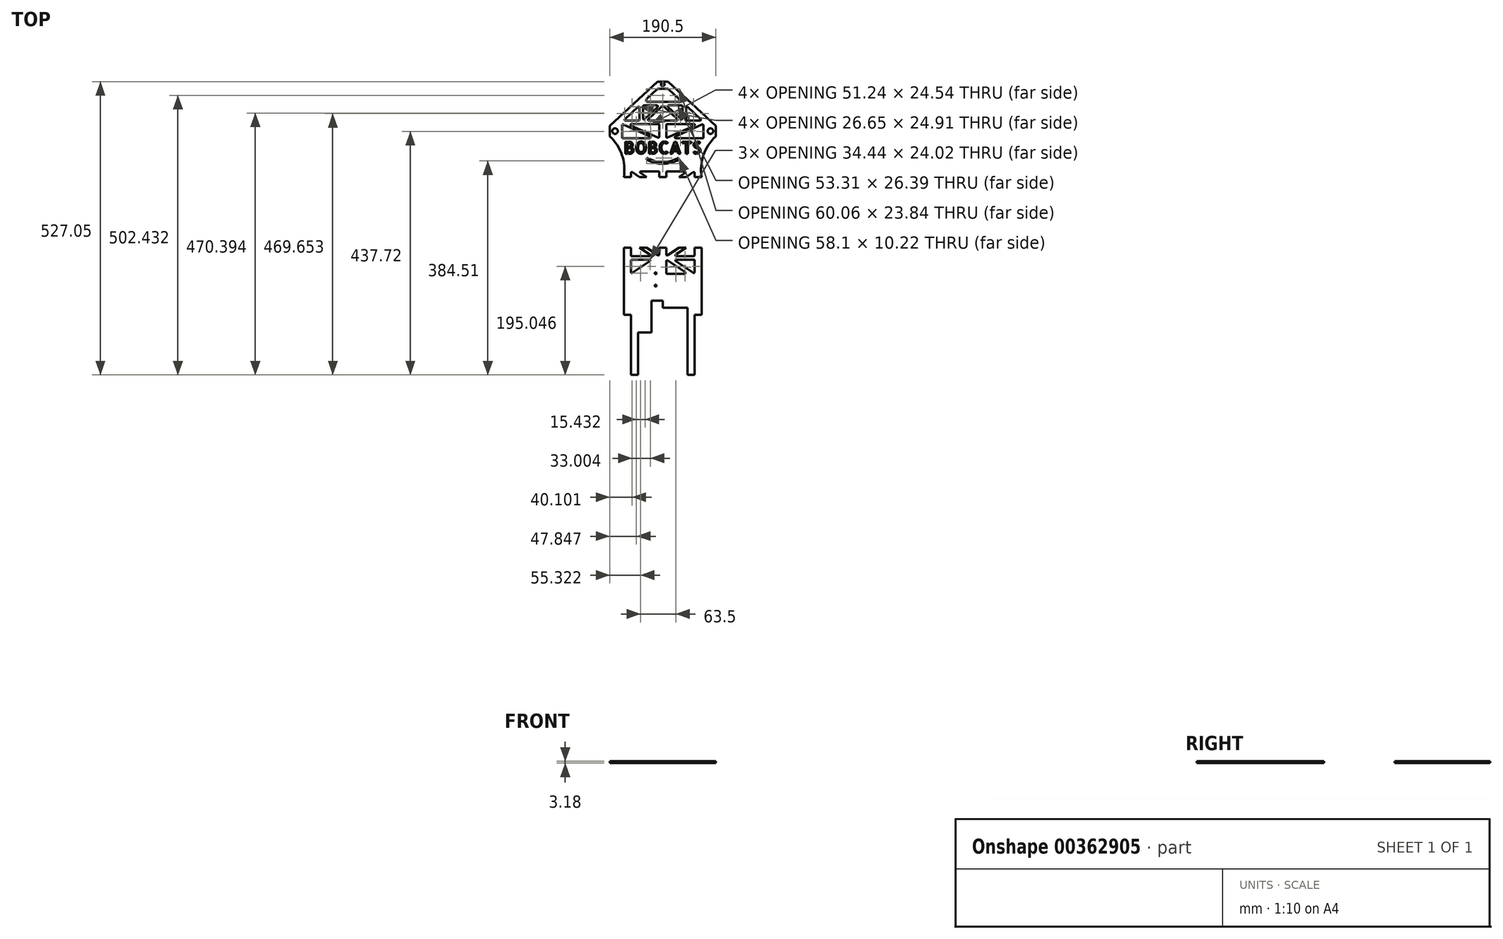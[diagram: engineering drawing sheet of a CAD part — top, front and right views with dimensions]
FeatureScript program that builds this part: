
annotation { "Feature Type Name" : "Feature", "Feature Type Description" : "" }
export const myFeature = defineFeature(function(context is Context, id is Id, definition is map)
    precondition{}
    {
        {
            var Q0;
            Q0=qCreatedBy(makeId("Top.planeOp"),FACE);
            var sketch = newSketch(context, id + "F0", { "sketchPlane" : qUnion([Q0])});
            skLineSegment(sketch, "E0.bottom", {"start": v(0, 0) * mm, "end": v(139.7, 0) * mm});
            skLineSegment(sketch, "E0.left", {"start": v(0, 0) * mm, "end": v(0, 127) * mm});
            skLineSegment(sketch, "E0.right", {"start": v(139.7, 0) * mm, "end": v(139.7, 153) * mm});
            skLineSegment(sketch, "E1.top", {"start": v(12.7, -228.6) * mm, "end": v(25.4, -228.6) * mm});
            skLineSegment(sketch, "E1.left", {"start": v(0, 0) * mm, "end": v(0, -120.65) * mm});
            skLineSegment(sketch, "E1.right", {"start": v(139.7, 0) * mm, "end": v(139.7, -120.65) * mm});
            skPoint(sketch, "E1.middle", {"position": v(69.85, -114.3) * mm});
            skLineSegment(sketch, "E2.top", {"start": v(25.4, -152.4) * mm, "end": v(49.53, -152.4) * mm});
            skLineSegment(sketch, "E2.left", {"start": v(25.4, -228.6) * mm, "end": v(25.4, -152.4) * mm});
            skLineSegment(sketch, "E2.right", {"start": v(114.3, -228.6) * mm, "end": v(114.3, -152.4) * mm});
            skLineSegment(sketch, "E3.top", {"start": v(114.3, -107.95) * mm, "end": v(69.85, -107.95) * mm});
            skLineSegment(sketch, "E3.left", {"start": v(114.3, -152.4) * mm, "end": v(114.3, -107.95) * mm});
            skLineSegment(sketch, "E4.top", {"start": v(69.85, -95.25) * mm, "end": v(49.53, -95.25) * mm});
            skLineSegment(sketch, "E4.left", {"start": v(69.85, -107.95) * mm, "end": v(69.85, -95.25) * mm});
            skLineSegment(sketch, "E4.right", {"start": v(49.53, -152.4) * mm, "end": v(49.53, -95.25) * mm});
            skLineSegment(sketch, "E5.left", {"start": v(25.4, -228.6) * mm, "end": v(25.4, -222.25) * mm});
            skLineSegment(sketch, "E5.right", {"start": v(114.3, -107.11) * mm, "end": v(114.3, -100.76) * mm});
            skPoint(sketch, "E6", {"position": v(57.15, -46.04) * mm});
            skPoint(sketch, "E7", {"position": v(57.15, -68.26) * mm});
            skCircle(sketch, "E8", {"center": v(57.15, -68.26) * mm, "radius": 1.59 * mm});
            skCircle(sketch, "E9", {"center": v(57.15, -46.04) * mm, "radius": 1.59 * mm});
            skLineSegment(sketch, "E10.top", {"start": v(0, -120.65) * mm, "end": v(12.7, -120.65) * mm});
            skLineSegment(sketch, "E10.right", {"start": v(12.7, -228.6) * mm, "end": v(12.7, -120.65) * mm});
            skPoint(sketch, "E11.oppositeSnap0", {"position": v(59.7, -152.4) * mm});
            skLineSegment(sketch, "E12.top", {"start": v(127, -120.65) * mm, "end": v(139.7, -120.65) * mm});
            skLineSegment(sketch, "E12.left", {"start": v(127, -228.6) * mm, "end": v(127, -120.65) * mm});
            skPoint(sketch, "E13.orphan", {"position": v(0, -228.6) * mm});
            skPoint(sketch, "E14.orphan", {"position": v(139.7, -228.6) * mm});
            skLineSegment(sketch, "E15.trimOffspring", {"start": v(114.3, -228.6) * mm, "end": v(127, -228.6) * mm});
            skPoint(sketch, "E3.bottom.end.orphan", {"position": v(69.85, -152.4) * mm});
            skLineSegment(sketch, "E16.bottom", {"start": v(60.32, 298.45) * mm, "end": v(79.38, 298.45) * mm});
            skLineSegment(sketch, "E16.top", {"start": v(0, 127) * mm, "end": v(139.7, 127) * mm});
            skLineSegment(sketch, "E16.left", {"start": v(-25.4, 219.08) * mm, "end": v(-25.4, 200.02) * mm});
            skLineSegment(sketch, "E16.right", {"start": v(165.1, 219.08) * mm, "end": v(165.1, 200.02) * mm});
            skLineSegment(sketch, "E17", {"start": v(60.32, 298.45) * mm, "end": v(-25.4, 219.08) * mm});
            skLineSegment(sketch, "E18", {"start": v(79.38, 298.45) * mm, "end": v(165.1, 219.08) * mm});
            skPoint(sketch, "E19", {"position": v(69.85, 293.37) * mm});
            skPoint(sketch, "E19.positionSnap0", {"position": v(69.85, 298.45) * mm});
            skCircle(sketch, "E20", {"center": v(69.85, 293.37) * mm, "radius": 3.2 * mm});
            skLineSegment(sketch, "E21.bottom", {"start": v(64.34, 298.45) * mm, "end": v(74.5, 298.45) * mm});
            skPoint(sketch, "E22", {"position": v(69.85, 127) * mm});
            skPoint(sketch, "E23", {"position": v(-25.4, 209.55) * mm});
            skPoint(sketch, "E24", {"position": v(165.1, 209.55) * mm});
            skText(sketch, "E25", { "text": "BOBCATS", "fontName": "AllertaStencil-Regular.ttf"});
            skArc(sketch, "E26", {"start": v(0, 127) * mm, "mid": v(-3.47, 166.72) * mm, "end": v(-25.4, 200.03) * mm});
            skLineSegment(sketch, "E27", {"start": v(42.39, 159.43) * mm, "end": v(100.33, 159.43) * mm, "construction": true});
            skArc(sketch, "E28", {"start": v(42.39, 159.43) * mm, "mid": v(69.85, 152.4) * mm, "end": v(97.31, 159.43) * mm, "construction": true});
            skArc(sketch, "E29.0", {"start": v(43.16, 160.83) * mm, "mid": v(69.85, 154) * mm, "end": v(96.54, 160.83) * mm});
            skArc(sketch, "E30.0", {"start": v(41.62, 158.03) * mm, "mid": v(69.85, 150.8) * mm, "end": v(98.08, 158.03) * mm});
            skCircle(sketch, "E31", {"center": v(42.39, 159.43) * mm, "radius": 1.6 * mm});
            skCircle(sketch, "E32", {"center": v(97.31, 159.43) * mm, "radius": 1.6 * mm});
            skLineSegment(sketch, "E33", {"start": v(59.72, 284.9) * mm, "end": v(40.83, 267.42) * mm});
            skLineSegment(sketch, "E34", {"start": v(42.99, 261.91) * mm, "end": v(96.71, 261.91) * mm});
            skLineSegment(sketch, "E35", {"start": v(98.87, 267.42) * mm, "end": v(79.98, 284.9) * mm});
            skLineSegment(sketch, "E36", {"start": v(77.83, 285.75) * mm, "end": v(61.87, 285.75) * mm});
            skPoint(sketch, "E37.visualSharp", {"position": v(60.63, 285.75) * mm});
            skArc(sketch, "E37.filletArc", {"start": v(61.87, 285.75) * mm, "mid": v(60.71, 285.53) * mm, "end": v(59.72, 284.9) * mm});
            skPoint(sketch, "E38.visualSharp", {"position": v(79.07, 285.75) * mm});
            skArc(sketch, "E38.filletArc", {"start": v(79.98, 284.9) * mm, "mid": v(78.99, 285.53) * mm, "end": v(77.83, 285.75) * mm});
            skPoint(sketch, "E39.visualSharp", {"position": v(34.89, 261.91) * mm});
            skArc(sketch, "E39.filletArc", {"start": v(40.83, 267.42) * mm, "mid": v(40.03, 263.93) * mm, "end": v(42.99, 261.91) * mm});
            skPoint(sketch, "E40.visualSharp", {"position": v(104.81, 261.91) * mm});
            skArc(sketch, "E40.filletArc", {"start": v(96.71, 261.91) * mm, "mid": v(99.67, 263.93) * mm, "end": v(98.87, 267.42) * mm});
            skCircle(sketch, "E41", {"center": v(-15.88, 209.55) * mm, "radius": 5 * mm});
            skCircle(sketch, "E42", {"center": v(155.58, 209.55) * mm, "radius": 5 * mm});
            skLineSegment(sketch, "E43", {"start": v(-3.18, 198.44) * mm, "end": v(-3.18, 219.8) * mm});
            skLineSegment(sketch, "E44", {"start": v(-0.94, 221.26) * mm, "end": v(47.14, 199.89) * mm});
            skLineSegment(sketch, "E45", {"start": v(46.5, 196.85) * mm, "end": v(-1.59, 196.85) * mm});
            skLineSegment(sketch, "E46", {"start": v(13.19, 219.21) * mm, "end": v(61.27, 197.84) * mm});
            skLineSegment(sketch, "E47", {"start": v(63.5, 199.3) * mm, "end": v(63.5, 220.66) * mm});
            skLineSegment(sketch, "E48", {"start": v(61.91, 222.25) * mm, "end": v(13.83, 222.25) * mm});
            skLineSegment(sketch, "E49", {"start": v(142.88, 198.44) * mm, "end": v(142.88, 219.8) * mm});
            skLineSegment(sketch, "E50", {"start": v(140.64, 221.26) * mm, "end": v(92.56, 199.89) * mm});
            skLineSegment(sketch, "E51", {"start": v(93.2, 196.85) * mm, "end": v(141.29, 196.85) * mm});
            skLineSegment(sketch, "E52", {"start": v(76.2, 199.3) * mm, "end": v(76.2, 220.66) * mm});
            skLineSegment(sketch, "E53", {"start": v(78.43, 197.84) * mm, "end": v(126.51, 219.21) * mm});
            skLineSegment(sketch, "E54", {"start": v(125.87, 222.25) * mm, "end": v(77.79, 222.25) * mm});
            skPoint(sketch, "E55.visualSharp", {"position": v(6.35, 222.25) * mm});
            skArc(sketch, "E55.filletArc", {"start": v(13.83, 222.25) * mm, "mid": v(12.28, 221) * mm, "end": v(13.19, 219.21) * mm});
            skPoint(sketch, "E56.visualSharp", {"position": v(53.98, 196.85) * mm});
            skArc(sketch, "E56.filletArc", {"start": v(46.5, 196.85) * mm, "mid": v(48.05, 198.1) * mm, "end": v(47.14, 199.89) * mm});
            skPoint(sketch, "E57.visualSharp", {"position": v(-3.18, 222.25) * mm});
            skArc(sketch, "E57.filletArc", {"start": v(-0.94, 221.26) * mm, "mid": v(-2.45, 221.14) * mm, "end": v(-3.18, 219.8) * mm});
            skPoint(sketch, "E58.visualSharp", {"position": v(-3.18, 196.85) * mm});
            skArc(sketch, "E58.filletArc", {"start": v(-3.18, 198.44) * mm, "mid": v(-2.71, 197.31) * mm, "end": v(-1.59, 196.85) * mm});
            skPoint(sketch, "E59.visualSharp", {"position": v(76.2, 222.25) * mm});
            skArc(sketch, "E59.filletArc", {"start": v(77.79, 222.25) * mm, "mid": v(76.66, 221.79) * mm, "end": v(76.2, 220.66) * mm});
            skPoint(sketch, "E60.visualSharp", {"position": v(63.5, 222.25) * mm});
            skArc(sketch, "E60.filletArc", {"start": v(63.5, 220.66) * mm, "mid": v(63.04, 221.79) * mm, "end": v(61.91, 222.25) * mm});
            skPoint(sketch, "E61.visualSharp", {"position": v(63.5, 196.85) * mm});
            skArc(sketch, "E61.filletArc", {"start": v(61.27, 197.84) * mm, "mid": v(62.78, 197.96) * mm, "end": v(63.5, 199.3) * mm});
            skPoint(sketch, "E62.visualSharp", {"position": v(76.2, 196.85) * mm});
            skArc(sketch, "E62.filletArc", {"start": v(76.2, 199.3) * mm, "mid": v(76.92, 197.96) * mm, "end": v(78.43, 197.84) * mm});
            skPoint(sketch, "E63.visualSharp", {"position": v(133.35, 222.25) * mm});
            skArc(sketch, "E63.filletArc", {"start": v(126.51, 219.21) * mm, "mid": v(127.42, 221) * mm, "end": v(125.87, 222.25) * mm});
            skPoint(sketch, "E64.visualSharp", {"position": v(85.72, 196.85) * mm});
            skArc(sketch, "E64.filletArc", {"start": v(92.56, 199.89) * mm, "mid": v(91.65, 198.1) * mm, "end": v(93.2, 196.85) * mm});
            skPoint(sketch, "E65.visualSharp", {"position": v(142.88, 222.25) * mm});
            skArc(sketch, "E65.filletArc", {"start": v(142.88, 219.8) * mm, "mid": v(142.15, 221.14) * mm, "end": v(140.64, 221.26) * mm});
            skPoint(sketch, "E66.visualSharp", {"position": v(142.88, 196.85) * mm});
            skArc(sketch, "E66.filletArc", {"start": v(141.29, 196.85) * mm, "mid": v(142.41, 197.31) * mm, "end": v(142.88, 198.44) * mm});
            skLineSegment(sketch, "E67", {"start": v(68.77, 254.57) * mm, "end": v(43.7, 231.35) * mm});
            skLineSegment(sketch, "E68", {"start": v(44.78, 228.6) * mm, "end": v(94.92, 228.6) * mm});
            skLineSegment(sketch, "E69", {"start": v(96, 231.35) * mm, "end": v(70.93, 254.57) * mm});
            skLineSegment(sketch, "E70", {"start": v(60.53, 252.81) * mm, "end": v(37.04, 231.07) * mm});
            skLineSegment(sketch, "E71", {"start": v(34.38, 232.23) * mm, "end": v(34.38, 253.98) * mm});
            skLineSegment(sketch, "E72", {"start": v(35.97, 255.56) * mm, "end": v(59.45, 255.56) * mm});
            skLineSegment(sketch, "E73", {"start": v(25.36, 253.1) * mm, "end": v(1.88, 231.35) * mm});
            skLineSegment(sketch, "E74", {"start": v(2.96, 228.6) * mm, "end": v(26.44, 228.6) * mm});
            skLineSegment(sketch, "E75", {"start": v(28.03, 230.19) * mm, "end": v(28.03, 251.93) * mm});
            skPoint(sketch, "E76.visualSharp", {"position": v(28.03, 255.56) * mm});
            skArc(sketch, "E76.filletArc", {"start": v(28.03, 251.93) * mm, "mid": v(27.08, 253.39) * mm, "end": v(25.36, 253.1) * mm});
            skPoint(sketch, "E77.visualSharp", {"position": v(-1.1, 228.6) * mm});
            skArc(sketch, "E77.filletArc", {"start": v(1.88, 231.35) * mm, "mid": v(1.48, 229.6) * mm, "end": v(2.96, 228.6) * mm});
            skPoint(sketch, "E78.visualSharp", {"position": v(28.03, 228.6) * mm});
            skArc(sketch, "E78.filletArc", {"start": v(26.44, 228.6) * mm, "mid": v(27.56, 229.06) * mm, "end": v(28.03, 230.19) * mm});
            skPoint(sketch, "E79.visualSharp", {"position": v(34.38, 228.6) * mm});
            skArc(sketch, "E79.filletArc", {"start": v(34.38, 232.23) * mm, "mid": v(35.33, 230.78) * mm, "end": v(37.04, 231.07) * mm});
            skPoint(sketch, "E80.visualSharp", {"position": v(34.38, 255.56) * mm});
            skArc(sketch, "E80.filletArc", {"start": v(35.97, 255.56) * mm, "mid": v(34.84, 255.1) * mm, "end": v(34.38, 253.98) * mm});
            skPoint(sketch, "E81.visualSharp", {"position": v(63.5, 255.56) * mm});
            skArc(sketch, "E81.filletArc", {"start": v(60.53, 252.81) * mm, "mid": v(60.93, 254.56) * mm, "end": v(59.45, 255.56) * mm});
            skPoint(sketch, "E82.visualSharp", {"position": v(69.85, 255.56) * mm});
            skArc(sketch, "E82.filletArc", {"start": v(70.93, 254.57) * mm, "mid": v(69.85, 254.99) * mm, "end": v(68.77, 254.57) * mm});
            skPoint(sketch, "E83.visualSharp", {"position": v(40.73, 228.6) * mm});
            skArc(sketch, "E83.filletArc", {"start": v(43.7, 231.35) * mm, "mid": v(43.3, 229.6) * mm, "end": v(44.78, 228.6) * mm});
            skPoint(sketch, "E84.visualSharp", {"position": v(98.97, 228.6) * mm});
            skArc(sketch, "E84.filletArc", {"start": v(94.92, 228.6) * mm, "mid": v(96.4, 229.6) * mm, "end": v(96, 231.35) * mm});
            skLineSegment(sketch, "E85", {"start": v(69.85, 260.44) * mm, "end": v(69.85, 219.43) * mm});
            skLineSegment(sketch, "E86.MirrorCS", {"start": v(79.17, 252.81) * mm, "end": v(102.66, 231.07) * mm});
            skLineSegment(sketch, "E87.MirrorCS", {"start": v(103.73, 255.56) * mm, "end": v(80.25, 255.56) * mm});
            skLineSegment(sketch, "E88.MirrorCS", {"start": v(105.32, 232.23) * mm, "end": v(105.32, 253.98) * mm});
            skLineSegment(sketch, "E89.MirrorCS", {"start": v(111.67, 230.19) * mm, "end": v(111.67, 251.93) * mm});
            skLineSegment(sketch, "E90.MirrorCS", {"start": v(114.34, 253.1) * mm, "end": v(137.82, 231.35) * mm});
            skLineSegment(sketch, "E91.MirrorCS", {"start": v(136.74, 228.6) * mm, "end": v(113.26, 228.6) * mm});
            skArc(sketch, "E92.MirrorCS", {"start": v(111.67, 251.93) * mm, "mid": v(112.62, 253.39) * mm, "end": v(114.34, 253.1) * mm});
            skArc(sketch, "E93.MirrorCS", {"start": v(113.26, 228.6) * mm, "mid": v(112.14, 229.06) * mm, "end": v(111.67, 230.19) * mm});
            skArc(sketch, "E94.MirrorCS", {"start": v(105.32, 232.23) * mm, "mid": v(104.37, 230.78) * mm, "end": v(102.66, 231.07) * mm});
            skArc(sketch, "E95.MirrorCS", {"start": v(103.73, 255.56) * mm, "mid": v(104.86, 255.1) * mm, "end": v(105.32, 253.98) * mm});
            skArc(sketch, "E96.MirrorCS", {"start": v(79.17, 252.81) * mm, "mid": v(78.77, 254.56) * mm, "end": v(80.25, 255.56) * mm});
            skArc(sketch, "E97.MirrorCS", {"start": v(137.82, 231.35) * mm, "mid": v(138.22, 229.6) * mm, "end": v(136.74, 228.6) * mm});
            skLineSegment(sketch, "E98", {"start": v(12.7, 113.4) * mm, "end": v(12.7, 134.24) * mm});
            skLineSegment(sketch, "E99", {"start": v(15.17, 135.56) * mm, "end": v(46.44, 114.71) * mm});
            skLineSegment(sketch, "E100", {"start": v(45.56, 111.8) * mm, "end": v(14.29, 111.8) * mm});
            skLineSegment(sketch, "E101", {"start": v(29.76, 134.3) * mm, "end": v(61.03, 113.45) * mm});
            skLineSegment(sketch, "E102", {"start": v(63.5, 114.77) * mm, "end": v(63.5, 135.62) * mm});
            skLineSegment(sketch, "E103", {"start": v(61.91, 137.2) * mm, "end": v(30.64, 137.2) * mm});
            skLineSegment(sketch, "E104", {"start": v(76.2, 135.62) * mm, "end": v(76.2, 114.77) * mm});
            skLineSegment(sketch, "E105", {"start": v(78.67, 113.45) * mm, "end": v(109.94, 134.3) * mm});
            skLineSegment(sketch, "E106", {"start": v(109.06, 137.2) * mm, "end": v(77.79, 137.2) * mm});
            skLineSegment(sketch, "E107", {"start": v(124.53, 135.56) * mm, "end": v(93.26, 114.71) * mm});
            skLineSegment(sketch, "E108", {"start": v(94.14, 111.8) * mm, "end": v(125.41, 111.8) * mm});
            skLineSegment(sketch, "E109", {"start": v(127, 113.4) * mm, "end": v(127, 134.24) * mm});
            skArc(sketch, "E110.MirrorCS", {"start": v(139.7, 127) * mm, "mid": v(143.17, 166.72) * mm, "end": v(165.1, 200.03) * mm});
            skLineSegment(sketch, "E111", {"start": v(14.29, 105.46) * mm, "end": v(45.56, 105.46) * mm});
            skLineSegment(sketch, "E112", {"start": v(46.44, 102.55) * mm, "end": v(15.17, 81.7) * mm});
            skLineSegment(sketch, "E113", {"start": v(12.7, 83.02) * mm, "end": v(12.7, 103.87) * mm});
            skLineSegment(sketch, "E114", {"start": v(63.5, 102.61) * mm, "end": v(63.5, 81.64) * mm});
            skLineSegment(sketch, "E115", {"start": v(61.91, 80.06) * mm, "end": v(27.83, 80.06) * mm});
            skLineSegment(sketch, "E116", {"start": v(27, 83) * mm, "end": v(61.08, 103.97) * mm});
            skLineSegment(sketch, "E117", {"start": v(76.2, 102.49) * mm, "end": v(76.2, 81.64) * mm});
            skLineSegment(sketch, "E118", {"start": v(77.79, 80.06) * mm, "end": v(109.06, 80.06) * mm});
            skLineSegment(sketch, "E119", {"start": v(109.94, 82.96) * mm, "end": v(78.67, 103.8) * mm});
            skLineSegment(sketch, "E120", {"start": v(93.26, 102.55) * mm, "end": v(124.53, 81.7) * mm});
            skLineSegment(sketch, "E121", {"start": v(127, 83.02) * mm, "end": v(127, 103.87) * mm});
            skLineSegment(sketch, "E122", {"start": v(125.41, 105.46) * mm, "end": v(94.14, 105.46) * mm});
            skPoint(sketch, "E123.visualSharp", {"position": v(12.7, 111.8) * mm});
            skArc(sketch, "E123.filletArc", {"start": v(12.7, 113.4) * mm, "mid": v(13.16, 112.27) * mm, "end": v(14.29, 111.8) * mm});
            skPoint(sketch, "E124.visualSharp", {"position": v(50.8, 111.8) * mm});
            skArc(sketch, "E124.filletArc", {"start": v(45.56, 111.8) * mm, "mid": v(47.08, 112.93) * mm, "end": v(46.44, 114.71) * mm});
            skPoint(sketch, "E125.visualSharp", {"position": v(12.7, 137.2) * mm});
            skArc(sketch, "E125.filletArc", {"start": v(15.17, 135.56) * mm, "mid": v(13.54, 135.64) * mm, "end": v(12.7, 134.24) * mm});
            skPoint(sketch, "E126.visualSharp", {"position": v(25.4, 137.2) * mm});
            skArc(sketch, "E126.filletArc", {"start": v(30.64, 137.2) * mm, "mid": v(29.12, 136.08) * mm, "end": v(29.76, 134.3) * mm});
            skPoint(sketch, "E127.visualSharp", {"position": v(63.5, 137.2) * mm});
            skArc(sketch, "E127.filletArc", {"start": v(63.5, 135.62) * mm, "mid": v(63.04, 136.74) * mm, "end": v(61.91, 137.2) * mm});
            skPoint(sketch, "E128.visualSharp", {"position": v(63.5, 111.8) * mm});
            skArc(sketch, "E128.filletArc", {"start": v(61.03, 113.45) * mm, "mid": v(62.66, 113.37) * mm, "end": v(63.5, 114.77) * mm});
            skPoint(sketch, "E129.visualSharp", {"position": v(76.2, 111.8) * mm});
            skArc(sketch, "E129.filletArc", {"start": v(76.2, 114.77) * mm, "mid": v(77.04, 113.37) * mm, "end": v(78.67, 113.45) * mm});
            skPoint(sketch, "E130.visualSharp", {"position": v(114.3, 137.2) * mm});
            skArc(sketch, "E130.filletArc", {"start": v(109.94, 134.3) * mm, "mid": v(110.58, 136.08) * mm, "end": v(109.06, 137.2) * mm});
            skPoint(sketch, "E131.visualSharp", {"position": v(76.2, 137.2) * mm});
            skArc(sketch, "E131.filletArc", {"start": v(77.79, 137.2) * mm, "mid": v(76.66, 136.74) * mm, "end": v(76.2, 135.62) * mm});
            skPoint(sketch, "E132.visualSharp", {"position": v(127, 137.2) * mm});
            skArc(sketch, "E132.filletArc", {"start": v(127, 134.24) * mm, "mid": v(126.16, 135.64) * mm, "end": v(124.53, 135.56) * mm});
            skPoint(sketch, "E133.visualSharp", {"position": v(88.9, 111.8) * mm});
            skArc(sketch, "E133.filletArc", {"start": v(93.26, 114.71) * mm, "mid": v(92.62, 112.93) * mm, "end": v(94.14, 111.8) * mm});
            skPoint(sketch, "E134.visualSharp", {"position": v(127, 111.8) * mm});
            skArc(sketch, "E134.filletArc", {"start": v(125.41, 111.8) * mm, "mid": v(126.54, 112.27) * mm, "end": v(127, 113.4) * mm});
            skPoint(sketch, "E135.visualSharp", {"position": v(12.7, 105.46) * mm});
            skArc(sketch, "E135.filletArc", {"start": v(14.29, 105.46) * mm, "mid": v(13.16, 105) * mm, "end": v(12.7, 103.87) * mm});
            skPoint(sketch, "E136.visualSharp", {"position": v(50.8, 105.46) * mm});
            skArc(sketch, "E136.filletArc", {"start": v(46.44, 102.55) * mm, "mid": v(47.08, 104.33) * mm, "end": v(45.56, 105.46) * mm});
            skPoint(sketch, "E137.visualSharp", {"position": v(63.5, 105.46) * mm});
            skArc(sketch, "E137.filletArc", {"start": v(63.5, 102.61) * mm, "mid": v(62.69, 104) * mm, "end": v(61.08, 103.97) * mm});
            skPoint(sketch, "E138.visualSharp", {"position": v(63.5, 80.06) * mm});
            skArc(sketch, "E138.filletArc", {"start": v(61.91, 80.06) * mm, "mid": v(63.04, 80.52) * mm, "end": v(63.5, 81.64) * mm});
            skPoint(sketch, "E139.visualSharp", {"position": v(22.23, 80.06) * mm});
            skArc(sketch, "E139.filletArc", {"start": v(27, 83) * mm, "mid": v(26.3, 81.21) * mm, "end": v(27.83, 80.06) * mm});
            skPoint(sketch, "E140.visualSharp", {"position": v(76.2, 80.06) * mm});
            skArc(sketch, "E140.filletArc", {"start": v(76.2, 81.64) * mm, "mid": v(76.66, 80.52) * mm, "end": v(77.79, 80.06) * mm});
            skPoint(sketch, "E141.visualSharp", {"position": v(114.3, 80.06) * mm});
            skArc(sketch, "E141.filletArc", {"start": v(109.06, 80.06) * mm, "mid": v(110.58, 81.18) * mm, "end": v(109.94, 82.96) * mm});
            skPoint(sketch, "E142.visualSharp", {"position": v(76.2, 105.46) * mm});
            skArc(sketch, "E142.filletArc", {"start": v(78.67, 103.8) * mm, "mid": v(77.04, 103.89) * mm, "end": v(76.2, 102.49) * mm});
            skPoint(sketch, "E143.visualSharp", {"position": v(88.9, 105.46) * mm});
            skArc(sketch, "E143.filletArc", {"start": v(94.14, 105.46) * mm, "mid": v(92.62, 104.33) * mm, "end": v(93.26, 102.55) * mm});
            skPoint(sketch, "E144.visualSharp", {"position": v(127, 105.46) * mm});
            skArc(sketch, "E144.filletArc", {"start": v(127, 103.87) * mm, "mid": v(126.54, 105) * mm, "end": v(125.41, 105.46) * mm});
            skPoint(sketch, "E145.visualSharp", {"position": v(127, 80.06) * mm});
            skArc(sketch, "E145.filletArc", {"start": v(124.53, 81.7) * mm, "mid": v(126.16, 81.62) * mm, "end": v(127, 83.02) * mm});
            skPoint(sketch, "E146.visualSharp", {"position": v(12.7, 80.06) * mm});
            skArc(sketch, "E146.filletArc", {"start": v(12.7, 83.02) * mm, "mid": v(13.54, 81.62) * mm, "end": v(15.17, 81.7) * mm});
            skLineSegment(sketch, "E147.0.1.0", {"start": v(127, 19.52) * mm, "end": v(127, 40.37) * mm});
            skArc(sketch, "E147.0.1.1", {"start": v(109.06, 16.56) * mm, "mid": v(110.58, 17.68) * mm, "end": v(109.94, 19.46) * mm});
            skPoint(sketch, "E147.0.1.2", {"position": v(88.9, 41.96) * mm});
            skLineSegment(sketch, "E147.0.1.3", {"start": v(127, 49.9) * mm, "end": v(127, 70.74) * mm});
            skLineSegment(sketch, "E147.0.1.4", {"start": v(45.56, 48.3) * mm, "end": v(14.29, 48.3) * mm});
            skLineSegment(sketch, "E147.0.1.5", {"start": v(61.91, 73.7) * mm, "end": v(30.64, 73.7) * mm});
            skArc(sketch, "E147.0.1.6", {"start": v(94.14, 41.96) * mm, "mid": v(92.62, 40.83) * mm, "end": v(93.26, 39.05) * mm});
            skLineSegment(sketch, "E147.0.1.7", {"start": v(77.79, 16.56) * mm, "end": v(109.06, 16.56) * mm});
            skPoint(sketch, "E147.0.1.8", {"position": v(127, 41.96) * mm});
            skPoint(sketch, "E147.0.1.9", {"position": v(76.2, 73.7) * mm});
            skPoint(sketch, "E147.0.1.10", {"position": v(127, 16.56) * mm});
            skPoint(sketch, "E147.0.1.11", {"position": v(63.5, 41.96) * mm});
            skArc(sketch, "E147.0.1.12", {"start": v(45.56, 48.3) * mm, "mid": v(47.08, 49.43) * mm, "end": v(46.44, 51.21) * mm});
            skLineSegment(sketch, "E147.0.1.13", {"start": v(124.53, 72.06) * mm, "end": v(93.26, 51.21) * mm});
            skPoint(sketch, "E147.0.1.14", {"position": v(22.23, 16.56) * mm});
            skPoint(sketch, "E147.0.1.15", {"position": v(63.5, 48.3) * mm});
            skArc(sketch, "E147.0.1.16", {"start": v(61.03, 49.95) * mm, "mid": v(62.66, 49.87) * mm, "end": v(63.5, 51.27) * mm});
            skPoint(sketch, "E147.0.1.17", {"position": v(25.4, 73.7) * mm});
            skPoint(sketch, "E147.0.1.18", {"position": v(63.5, 16.56) * mm});
            skLineSegment(sketch, "E147.0.1.19", {"start": v(61.91, 16.56) * mm, "end": v(27.83, 16.56) * mm});
            skLineSegment(sketch, "E147.0.1.20", {"start": v(29.76, 70.8) * mm, "end": v(61.03, 49.95) * mm});
            skLineSegment(sketch, "E147.0.1.21", {"start": v(63.5, 39.11) * mm, "end": v(63.5, 18.14) * mm});
            skPoint(sketch, "E147.0.1.22", {"position": v(76.2, 48.3) * mm});
            skLineSegment(sketch, "E147.0.1.23", {"start": v(125.41, 41.96) * mm, "end": v(94.14, 41.96) * mm});
            skPoint(sketch, "E147.0.1.24", {"position": v(12.7, 41.96) * mm});
            skArc(sketch, "E147.0.1.25", {"start": v(12.7, 19.52) * mm, "mid": v(13.54, 18.12) * mm, "end": v(15.17, 18.2) * mm});
            skPoint(sketch, "E147.0.1.26", {"position": v(69.85, 63.5) * mm});
            skLineSegment(sketch, "E147.0.1.27", {"start": v(27, 19.5) * mm, "end": v(61.08, 40.47) * mm});
            skLineSegment(sketch, "E147.0.1.28", {"start": v(63.5, 51.27) * mm, "end": v(63.5, 72.12) * mm});
            skPoint(sketch, "E147.0.1.29", {"position": v(12.7, 16.56) * mm});
            skPoint(sketch, "E147.0.1.30", {"position": v(76.2, 41.96) * mm});
            skArc(sketch, "E147.0.1.31", {"start": v(15.17, 72.06) * mm, "mid": v(13.54, 72.14) * mm, "end": v(12.7, 70.74) * mm});
            skPoint(sketch, "E147.0.1.32", {"position": v(127, 73.7) * mm});
            skArc(sketch, "E147.0.1.33", {"start": v(63.5, 39.11) * mm, "mid": v(62.69, 40.5) * mm, "end": v(61.08, 40.47) * mm});
            skLineSegment(sketch, "E147.0.1.34", {"start": v(14.29, 41.96) * mm, "end": v(45.56, 41.96) * mm});
            skLineSegment(sketch, "E147.0.1.35", {"start": v(109.06, 73.7) * mm, "end": v(77.79, 73.7) * mm});
            skPoint(sketch, "E147.0.1.36", {"position": v(114.3, 16.56) * mm});
            skLineSegment(sketch, "E147.0.1.37", {"start": v(46.44, 39.05) * mm, "end": v(15.17, 18.2) * mm});
            skPoint(sketch, "E147.0.1.38", {"position": v(63.5, 73.7) * mm});
            skPoint(sketch, "E147.0.1.39", {"position": v(76.2, 16.56) * mm});
            skArc(sketch, "E147.0.1.40", {"start": v(124.53, 18.2) * mm, "mid": v(126.16, 18.12) * mm, "end": v(127, 19.52) * mm});
            skPoint(sketch, "E147.0.1.41", {"position": v(12.7, 73.7) * mm});
            skPoint(sketch, "E147.0.1.42", {"position": v(50.8, 48.3) * mm});
            skLineSegment(sketch, "E147.0.1.43", {"start": v(94.14, 48.3) * mm, "end": v(125.41, 48.3) * mm});
            skPoint(sketch, "E147.0.1.44", {"position": v(88.9, 48.3) * mm});
            skLineSegment(sketch, "E147.0.1.45", {"start": v(12.7, 49.9) * mm, "end": v(12.7, 70.74) * mm});
            skPoint(sketch, "E147.0.1.46", {"position": v(114.3, 73.7) * mm});
            skPoint(sketch, "E147.0.1.47", {"position": v(50.8, 41.96) * mm});
            skLineSegment(sketch, "E147.0.1.48", {"start": v(109.94, 19.46) * mm, "end": v(78.67, 40.3) * mm});
            skArc(sketch, "E147.0.1.49", {"start": v(78.67, 40.3) * mm, "mid": v(77.04, 40.39) * mm, "end": v(76.2, 38.99) * mm});
            skPoint(sketch, "E147.0.1.50", {"position": v(127, 48.3) * mm});
            skArc(sketch, "E147.0.1.51", {"start": v(127, 70.74) * mm, "mid": v(126.16, 72.14) * mm, "end": v(124.53, 72.06) * mm});
            skLineSegment(sketch, "E147.0.1.52", {"start": v(93.26, 39.05) * mm, "end": v(124.53, 18.2) * mm});
            skLineSegment(sketch, "E147.0.1.53", {"start": v(78.67, 49.95) * mm, "end": v(109.94, 70.8) * mm});
            skArc(sketch, "E147.0.1.54", {"start": v(46.44, 39.05) * mm, "mid": v(47.08, 40.83) * mm, "end": v(45.56, 41.96) * mm});
            skLineSegment(sketch, "E147.0.1.55", {"start": v(15.17, 72.06) * mm, "end": v(46.44, 51.21) * mm});
            skArc(sketch, "E147.0.1.56", {"start": v(27, 19.5) * mm, "mid": v(26.3, 17.71) * mm, "end": v(27.83, 16.56) * mm});
            skArc(sketch, "E147.0.1.57", {"start": v(93.26, 51.21) * mm, "mid": v(92.62, 49.43) * mm, "end": v(94.14, 48.3) * mm});
            skPoint(sketch, "E147.0.1.58", {"position": v(12.7, 48.3) * mm});
            skLineSegment(sketch, "E147.0.1.59", {"start": v(76.2, 72.12) * mm, "end": v(76.2, 51.27) * mm});
            skLineSegment(sketch, "E147.0.1.60", {"start": v(76.2, 38.99) * mm, "end": v(76.2, 18.14) * mm});
            skLineSegment(sketch, "E147.0.1.61", {"start": v(12.7, 19.52) * mm, "end": v(12.7, 40.37) * mm});
            skArc(sketch, "E147.0.1.62", {"start": v(76.2, 51.27) * mm, "mid": v(77.04, 49.87) * mm, "end": v(78.67, 49.95) * mm});
            skArc(sketch, "E147.0.1.63", {"start": v(12.7, 49.9) * mm, "mid": v(13.16, 48.77) * mm, "end": v(14.29, 48.3) * mm});
            skArc(sketch, "E147.0.1.64", {"start": v(14.29, 41.96) * mm, "mid": v(13.16, 41.5) * mm, "end": v(12.7, 40.37) * mm});
            skArc(sketch, "E147.0.1.65", {"start": v(127, 40.37) * mm, "mid": v(126.54, 41.5) * mm, "end": v(125.41, 41.96) * mm});
            skArc(sketch, "E147.0.1.66", {"start": v(109.94, 70.8) * mm, "mid": v(110.58, 72.58) * mm, "end": v(109.06, 73.7) * mm});
            skArc(sketch, "E147.0.1.67", {"start": v(61.91, 16.56) * mm, "mid": v(63.04, 17.02) * mm, "end": v(63.5, 18.14) * mm});
            skArc(sketch, "E147.0.1.68", {"start": v(30.64, 73.7) * mm, "mid": v(29.12, 72.58) * mm, "end": v(29.76, 70.8) * mm});
            skArc(sketch, "E147.0.1.69", {"start": v(63.5, 72.12) * mm, "mid": v(63.04, 73.24) * mm, "end": v(61.91, 73.7) * mm});
            skArc(sketch, "E147.0.1.70", {"start": v(77.79, 73.7) * mm, "mid": v(76.66, 73.24) * mm, "end": v(76.2, 72.12) * mm});
            skArc(sketch, "E147.0.1.71", {"start": v(76.2, 18.14) * mm, "mid": v(76.66, 17.02) * mm, "end": v(77.79, 16.56) * mm});
            skArc(sketch, "E147.0.1.72", {"start": v(125.41, 48.3) * mm, "mid": v(126.54, 48.77) * mm, "end": v(127, 49.9) * mm});
            skLineSegment(sketch, "E147.0.2.0", {"start": v(127, -43.98) * mm, "end": v(127, -23.13) * mm});
            skArc(sketch, "E147.0.2.1", {"start": v(109.06, -46.94) * mm, "mid": v(110.58, -45.82) * mm, "end": v(109.94, -44.04) * mm});
            skPoint(sketch, "E147.0.2.2", {"position": v(88.9, -21.54) * mm});
            skLineSegment(sketch, "E147.0.2.3", {"start": v(127, -13.6) * mm, "end": v(127, 7.24) * mm});
            skLineSegment(sketch, "E147.0.2.4", {"start": v(45.56, -15.2) * mm, "end": v(14.29, -15.2) * mm});
            skLineSegment(sketch, "E147.0.2.5", {"start": v(61.91, 10.2) * mm, "end": v(30.64, 10.2) * mm});
            skArc(sketch, "E147.0.2.6", {"start": v(94.14, -21.54) * mm, "mid": v(92.62, -22.67) * mm, "end": v(93.26, -24.45) * mm});
            skLineSegment(sketch, "E147.0.2.7", {"start": v(77.79, -46.94) * mm, "end": v(109.06, -46.94) * mm});
            skPoint(sketch, "E147.0.2.8", {"position": v(127, -21.54) * mm});
            skPoint(sketch, "E147.0.2.9", {"position": v(76.2, 10.2) * mm});
            skPoint(sketch, "E147.0.2.10", {"position": v(127, -46.94) * mm});
            skPoint(sketch, "E147.0.2.11", {"position": v(63.5, -21.54) * mm});
            skArc(sketch, "E147.0.2.12", {"start": v(45.56, -15.2) * mm, "mid": v(47.08, -14.07) * mm, "end": v(46.44, -12.29) * mm});
            skLineSegment(sketch, "E147.0.2.13", {"start": v(124.53, 8.56) * mm, "end": v(93.26, -12.29) * mm});
            skPoint(sketch, "E147.0.2.14", {"position": v(22.23, -46.94) * mm});
            skPoint(sketch, "E147.0.2.15", {"position": v(63.5, -15.2) * mm});
            skArc(sketch, "E147.0.2.16", {"start": v(61.03, -13.55) * mm, "mid": v(62.66, -13.63) * mm, "end": v(63.5, -12.23) * mm});
            skPoint(sketch, "E147.0.2.17", {"position": v(25.4, 10.2) * mm});
            skPoint(sketch, "E147.0.2.18", {"position": v(63.5, -46.94) * mm});
            skLineSegment(sketch, "E147.0.2.20", {"start": v(29.76, 7.3) * mm, "end": v(61.03, -13.55) * mm});
            skPoint(sketch, "E147.0.2.22", {"position": v(76.2, -15.2) * mm});
            skLineSegment(sketch, "E147.0.2.23", {"start": v(125.41, -21.54) * mm, "end": v(94.14, -21.54) * mm});
            skPoint(sketch, "E147.0.2.24", {"position": v(12.7, -21.54) * mm});
            skArc(sketch, "E147.0.2.25", {"start": v(12.7, -43.98) * mm, "mid": v(13.54, -45.38) * mm, "end": v(15.17, -45.3) * mm});
            skPoint(sketch, "E147.0.2.26", {"position": v(69.85, 0) * mm});
            skLineSegment(sketch, "E147.0.2.28", {"start": v(63.5, -12.23) * mm, "end": v(63.5, 8.62) * mm});
            skPoint(sketch, "E147.0.2.29", {"position": v(12.7, -46.94) * mm});
            skPoint(sketch, "E147.0.2.30", {"position": v(76.2, -21.54) * mm});
            skArc(sketch, "E147.0.2.31", {"start": v(15.17, 8.56) * mm, "mid": v(13.54, 8.64) * mm, "end": v(12.7, 7.24) * mm});
            skPoint(sketch, "E147.0.2.32", {"position": v(127, 10.2) * mm});
            skLineSegment(sketch, "E147.0.2.34", {"start": v(14.29, -21.54) * mm, "end": v(45.56, -21.54) * mm});
            skLineSegment(sketch, "E147.0.2.35", {"start": v(109.06, 10.2) * mm, "end": v(77.79, 10.2) * mm});
            skPoint(sketch, "E147.0.2.36", {"position": v(114.3, -46.94) * mm});
            skLineSegment(sketch, "E147.0.2.37", {"start": v(46.44, -24.45) * mm, "end": v(15.17, -45.3) * mm});
            skPoint(sketch, "E147.0.2.38", {"position": v(63.5, 10.2) * mm});
            skPoint(sketch, "E147.0.2.39", {"position": v(76.2, -46.94) * mm});
            skArc(sketch, "E147.0.2.40", {"start": v(124.53, -45.3) * mm, "mid": v(126.16, -45.38) * mm, "end": v(127, -43.98) * mm});
            skPoint(sketch, "E147.0.2.41", {"position": v(12.7, 10.2) * mm});
            skPoint(sketch, "E147.0.2.42", {"position": v(50.8, -15.2) * mm});
            skLineSegment(sketch, "E147.0.2.43", {"start": v(94.14, -15.2) * mm, "end": v(125.41, -15.2) * mm});
            skPoint(sketch, "E147.0.2.44", {"position": v(88.9, -15.2) * mm});
            skLineSegment(sketch, "E147.0.2.45", {"start": v(12.7, -13.6) * mm, "end": v(12.7, 7.24) * mm});
            skPoint(sketch, "E147.0.2.46", {"position": v(114.3, 10.2) * mm});
            skPoint(sketch, "E147.0.2.47", {"position": v(50.8, -21.54) * mm});
            skLineSegment(sketch, "E147.0.2.48", {"start": v(109.94, -44.04) * mm, "end": v(78.67, -23.2) * mm});
            skArc(sketch, "E147.0.2.49", {"start": v(78.67, -23.2) * mm, "mid": v(77.04, -23.11) * mm, "end": v(76.2, -24.51) * mm});
            skPoint(sketch, "E147.0.2.50", {"position": v(127, -15.2) * mm});
            skArc(sketch, "E147.0.2.51", {"start": v(127, 7.24) * mm, "mid": v(126.16, 8.64) * mm, "end": v(124.53, 8.56) * mm});
            skLineSegment(sketch, "E147.0.2.52", {"start": v(93.26, -24.45) * mm, "end": v(124.53, -45.3) * mm});
            skLineSegment(sketch, "E147.0.2.53", {"start": v(78.67, -13.55) * mm, "end": v(109.94, 7.3) * mm});
            skArc(sketch, "E147.0.2.54", {"start": v(46.44, -24.45) * mm, "mid": v(47.08, -22.67) * mm, "end": v(45.56, -21.54) * mm});
            skLineSegment(sketch, "E147.0.2.55", {"start": v(15.17, 8.56) * mm, "end": v(46.44, -12.29) * mm});
            skArc(sketch, "E147.0.2.57", {"start": v(93.26, -12.29) * mm, "mid": v(92.62, -14.07) * mm, "end": v(94.14, -15.2) * mm});
            skPoint(sketch, "E147.0.2.58", {"position": v(12.7, -15.2) * mm});
            skLineSegment(sketch, "E147.0.2.59", {"start": v(76.2, 8.62) * mm, "end": v(76.2, -12.23) * mm});
            skLineSegment(sketch, "E147.0.2.60", {"start": v(76.2, -24.51) * mm, "end": v(76.2, -45.36) * mm});
            skLineSegment(sketch, "E147.0.2.61", {"start": v(12.7, -43.98) * mm, "end": v(12.7, -23.13) * mm});
            skArc(sketch, "E147.0.2.62", {"start": v(76.2, -12.23) * mm, "mid": v(77.04, -13.63) * mm, "end": v(78.67, -13.55) * mm});
            skArc(sketch, "E147.0.2.63", {"start": v(12.7, -13.6) * mm, "mid": v(13.16, -14.73) * mm, "end": v(14.29, -15.2) * mm});
            skArc(sketch, "E147.0.2.64", {"start": v(14.29, -21.54) * mm, "mid": v(13.16, -22) * mm, "end": v(12.7, -23.13) * mm});
            skArc(sketch, "E147.0.2.65", {"start": v(127, -23.13) * mm, "mid": v(126.54, -22) * mm, "end": v(125.41, -21.54) * mm});
            skArc(sketch, "E147.0.2.66", {"start": v(109.94, 7.3) * mm, "mid": v(110.58, 9.08) * mm, "end": v(109.06, 10.2) * mm});
            skArc(sketch, "E147.0.2.68", {"start": v(30.64, 10.2) * mm, "mid": v(29.12, 9.08) * mm, "end": v(29.76, 7.3) * mm});
            skArc(sketch, "E147.0.2.69", {"start": v(63.5, 8.62) * mm, "mid": v(63.04, 9.74) * mm, "end": v(61.91, 10.2) * mm});
            skArc(sketch, "E147.0.2.70", {"start": v(77.79, 10.2) * mm, "mid": v(76.66, 9.74) * mm, "end": v(76.2, 8.62) * mm});
            skArc(sketch, "E147.0.2.71", {"start": v(76.2, -45.36) * mm, "mid": v(76.66, -46.48) * mm, "end": v(77.79, -46.94) * mm});
            skArc(sketch, "E147.0.2.72", {"start": v(125.41, -15.2) * mm, "mid": v(126.54, -14.73) * mm, "end": v(127, -13.6) * mm});
            skLineSegment(sketch, "E147.direction1", {"start": v(12.7, 80.06) * mm, "end": v(38.1, 80.06) * mm, "construction": true});
            skLineSegment(sketch, "E147.direction2", {"start": v(12.7, 80.06) * mm, "end": v(12.7, 16.56) * mm, "construction": true});
            const initialGuessF0  = {"E25": [0, 0.16896, 1, 0, 0.02154]};
            skSetInitialGuess(sketch, initialGuessF0);
            skSolve(sketch);
        }
        {
            var Q0;
            Q0=makeQuery(id+"F0.imprint","IMPRINT",FACE,{"disambiguationData":[TD([[makeQuery(id+"F0.imprint","IMPRINT",EDGE,{"derivedFrom":sQuery(id+"F0.wireOp",EDGE,"E0.left")}),-1.0]])]});
            var Q1;
            Q1=makeQuery(id+"F0.imprint","IMPRINT",FACE,{"disambiguationData":[TD([[makeQuery(id+"F0.imprint","IMPRINT",EDGE,{"derivedFrom":sQuery(id+"F0.wireOp",EDGE,"E0.bottom")}),-1.0]])]});
            var Q2;
            Q2=makeQuery(id+"F0.imprint","IMPRINT",FACE,{"disambiguationData":[TD([[makeQuery(id+"F0.imprint","IMPRINT",EDGE,{"derivedFrom":sQuery(id+"F0.wireOp",EDGE,"E16.top")}),1.0]])]});
            var Q3;
            Q3=makeQuery(id+"F0.imprint","IMPRINT",FACE,{"disambiguationData":[TD([[makeQuery(id+"F0.imprint","IMPRINT",EDGE,{"derivedFrom":sQuery(id+"F0.wireOp",EDGE,"E20")}),-1.0]])]});
            extrude(context, id + "F1", {"entities" : qUnion([Q0, Q1, Q2, Q3]), "depth" : 3.17 * mm});
        }
    });
